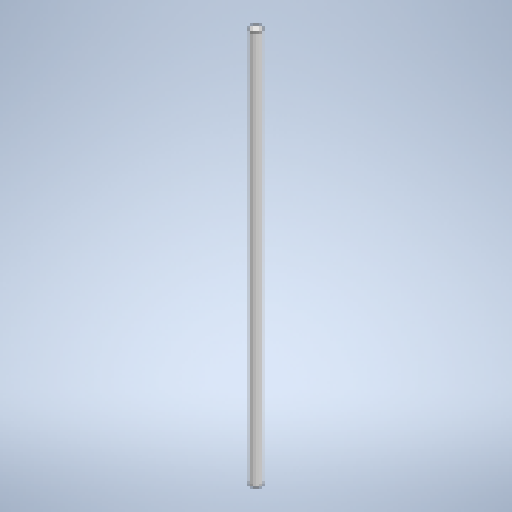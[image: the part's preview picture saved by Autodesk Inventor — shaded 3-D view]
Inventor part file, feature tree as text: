
AUTODESK INVENTOR PART (.ipt)
format: ipt  version: 2025 (Build 290162010, 162A)  size: 130,560 bytes
history: native  units: mm
features: extrude x1, sketch x1
ambient origin geometry x8: Origin, YZ Plane, XZ Plane, XY Plane, X Axis, Y Axis, Z Axis, Center Point
bodies: Solid1 (feature_tree)
feature tree (2):
  extrude  "Extrusion1"  Depth=720.0mm TaperAngle=0.0deg
  sketch  "Sketch1"  dims[d0=18.0mm d1=720.0mm d2=0.0mm]
